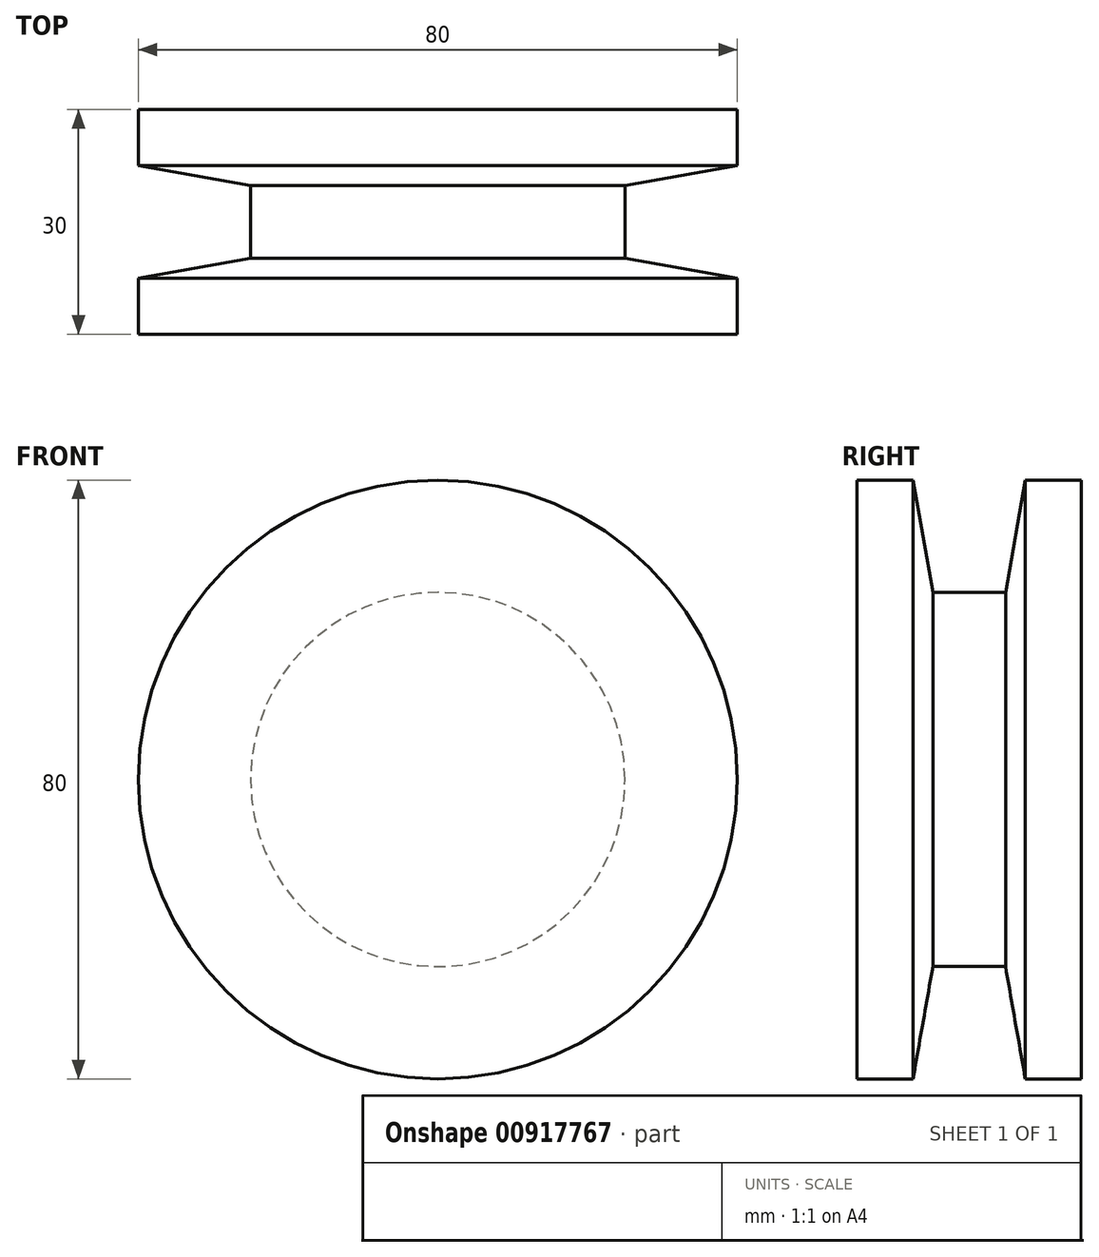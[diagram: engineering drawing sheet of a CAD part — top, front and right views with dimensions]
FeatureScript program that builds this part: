
annotation { "Feature Type Name" : "Feature", "Feature Type Description" : "" }
export const myFeature = defineFeature(function(context is Context, id is Id, definition is map)
    precondition{}
    {
        {
            var Q0;
            Q0=qCreatedBy(makeId("Right.planeOp"),FACE);
            var sketch = newSketch(context, id + "F0", { "sketchPlane" : qUnion([Q0])});
            skLineSegment(sketch, "E0", {"start": v(-15, 0) * mm, "end": v(15, 0) * mm});
            skLineSegment(sketch, "E1", {"start": v(-15, 0) * mm, "end": v(-15, 40) * mm});
            skLineSegment(sketch, "E2", {"start": v(-15, 40) * mm, "end": v(-7.5, 40) * mm});
            skLineSegment(sketch, "E3", {"start": v(-7.5, 40) * mm, "end": v(-4.86, 25) * mm});
            skLineSegment(sketch, "E4", {"start": v(-4.86, 25) * mm, "end": v(4.86, 25) * mm});
            skLineSegment(sketch, "E5", {"start": v(4.86, 25) * mm, "end": v(7.5, 40) * mm});
            skLineSegment(sketch, "E6", {"start": v(7.5, 40) * mm, "end": v(15, 40) * mm});
            skLineSegment(sketch, "E7", {"start": v(15, 40) * mm, "end": v(15, 0) * mm});
            skSolve(sketch);
        }
        {
            var Q0;
            Q0=makeQuery(id+"F0.imprint","IMPRINT",FACE,{"disambiguationData":[TD([[makeQuery(id+"F0.imprint","IMPRINT",EDGE,{"derivedFrom":sQuery(id+"F0.wireOp",EDGE,"E0")}),1.0]])]});
            var Q1;
            Q1=sQuery(id+"F0.wireOp",EDGE,"E0");
            revolve(context, id + "F1", {"surfaceOperationType" : NewSurfaceOperationType.NEW, "entities" : qUnion([Q0]), "axis" : qUnion([Q1]), "revolveType" : RevolveType.FULL});
        }
    });
